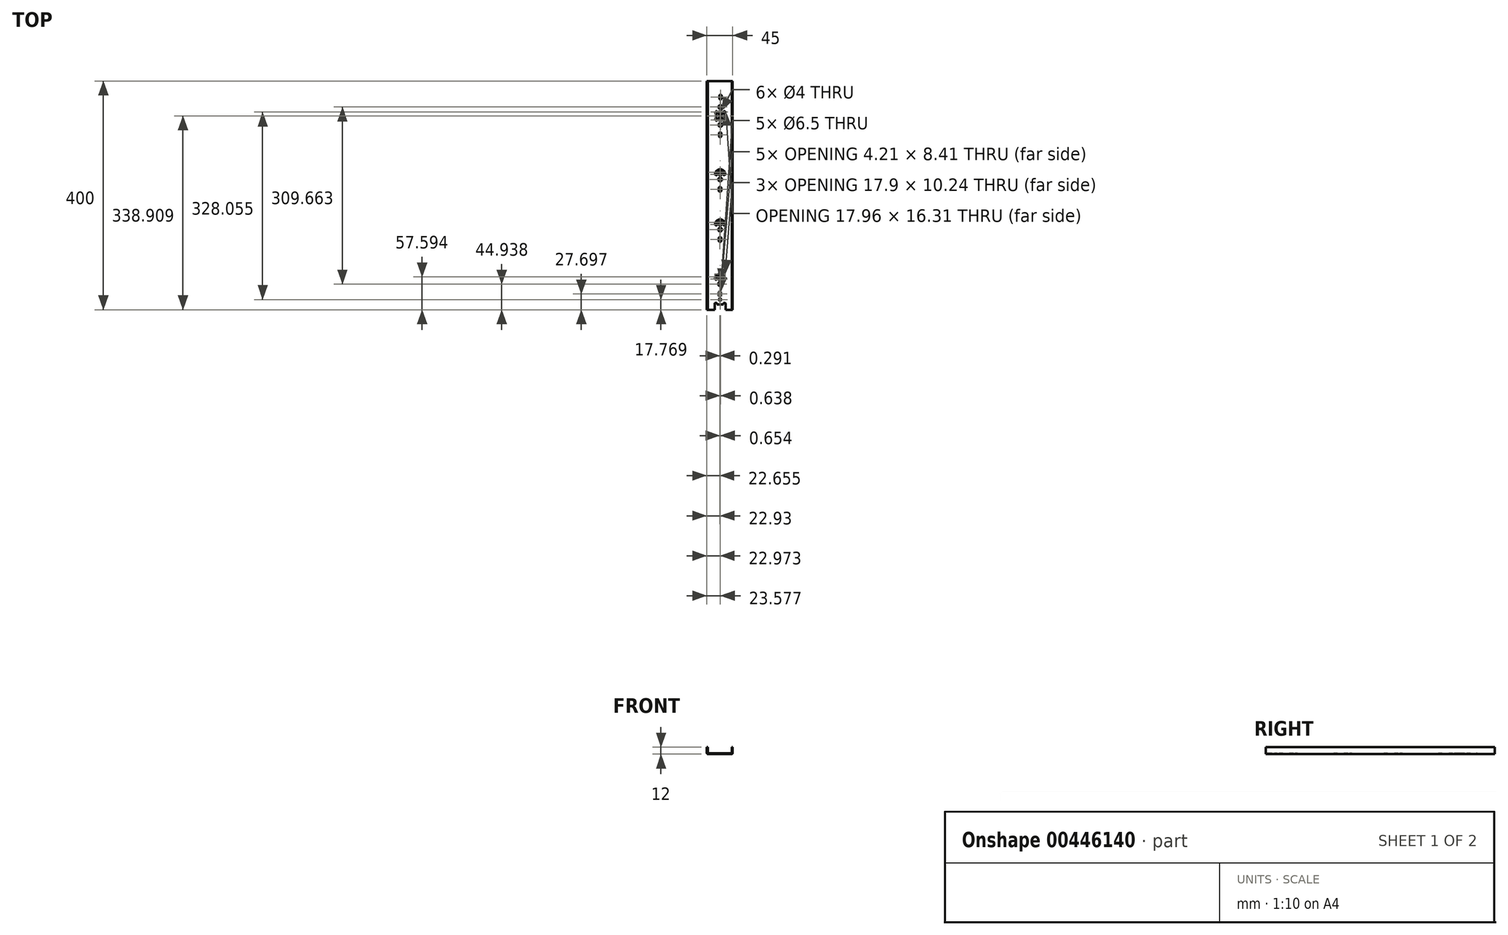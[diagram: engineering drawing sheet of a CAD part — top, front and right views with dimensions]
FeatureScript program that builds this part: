
annotation { "Feature Type Name" : "Feature", "Feature Type Description" : "" }
export const myFeature = defineFeature(function(context is Context, id is Id, definition is map)
    precondition{}
    {
        {
            var Q0;
            Q0=qCreatedBy(makeId("Front.planeOp"),FACE);
            var sketch = newSketch(context, id + "F0", { "sketchPlane" : qUnion([Q0])});
            skLineSegment(sketch, "E0", {"start": v(-48.01, 18) * mm, "end": v(-48.01, 8) * mm});
            skLineSegment(sketch, "E1", {"start": v(-5.01, 6) * mm, "end": v(-46.01, 6) * mm});
            skLineSegment(sketch, "E2", {"start": v(-3.01, 8) * mm, "end": v(-3.01, 18) * mm});
            skPoint(sketch, "E3.visualSharp", {"position": v(-48.01, 6) * mm});
            skArc(sketch, "E3.filletArc", {"start": v(-48.01, 8) * mm, "mid": v(-47.43, 6.59) * mm, "end": v(-46.01, 6) * mm});
            skPoint(sketch, "E4.visualSharp", {"position": v(-3.01, 6) * mm});
            skArc(sketch, "E4.filletArc", {"start": v(-5.01, 6) * mm, "mid": v(-3.6, 6.59) * mm, "end": v(-3.01, 8) * mm});
            skLineSegment(sketch, "E5.0", {"start": v(-46.52, 18) * mm, "end": v(-46.52, 8) * mm});
            skLineSegment(sketch, "E5.1", {"start": v(-4.5, 8) * mm, "end": v(-4.5, 18) * mm});
            skArc(sketch, "E5.2", {"start": v(-5.01, 7.5) * mm, "mid": v(-4.66, 7.64) * mm, "end": v(-4.5, 8) * mm});
            skLineSegment(sketch, "E5.3", {"start": v(-5.01, 7.5) * mm, "end": v(-46.01, 7.5) * mm});
            skArc(sketch, "E5.4", {"start": v(-46.52, 8) * mm, "mid": v(-46.37, 7.64) * mm, "end": v(-46.01, 7.5) * mm});
            skLineSegment(sketch, "E6", {"start": v(-48.01, 18) * mm, "end": v(-46.52, 18) * mm});
            skLineSegment(sketch, "E7", {"start": v(-4.5, 18) * mm, "end": v(-3.01, 18) * mm});
            skSolve(sketch);
        }
        {
            var Q0;
            Q0=makeQuery(id+"F0.imprint","IMPRINT",FACE,{"disambiguationData":[TD([[makeQuery(id+"F0.imprint","IMPRINT",EDGE,{"derivedFrom":sQuery(id+"F0.wireOp",EDGE,"E0")}),1.0]])]});
            extrude(context, id + "F1", {"entities" : qUnion([Q0]), "endBound" : BoundingType.SYMMETRIC, "depth" : 400 * mm});
        }
        {
            var Q0;
            Q0=qCreatedBy(makeId("Top.planeOp"),FACE);
            var sketch = newSketch(context, id + "F2", { "sketchPlane" : qUnion([Q0])});
            skLineSegment(sketch, "E8.top", {"start": v(-34.24, -200.48) * mm, "end": v(-15.31, -200.48) * mm});
            skLineSegment(sketch, "E8.left", {"start": v(-34.24, -189.04) * mm, "end": v(-34.24, -200.48) * mm});
            skLineSegment(sketch, "E8.right", {"start": v(-15.31, -189.04) * mm, "end": v(-15.31, -200.48) * mm});
            skPoint(sketch, "E8.middle", {"position": v(-24.78, -194.26) * mm});
            skLineSegment(sketch, "E9.top", {"start": v(-30.41, -190.8) * mm, "end": v(-18.97, -190.8) * mm});
            skLineSegment(sketch, "E9.left", {"start": v(-30.41, -189.04) * mm, "end": v(-30.41, -190.8) * mm});
            skLineSegment(sketch, "E9.right", {"start": v(-18.97, -189.04) * mm, "end": v(-18.97, -190.8) * mm});
            skLineSegment(sketch, "E10", {"start": v(-33.24, -188.04) * mm, "end": v(-31.41, -188.04) * mm});
            skLineSegment(sketch, "E11", {"start": v(-17.97, -188.04) * mm, "end": v(-16.31, -188.04) * mm});
            skPoint(sketch, "E12.visualSharp", {"position": v(-34.24, -188.04) * mm});
            skArc(sketch, "E12.filletArc", {"start": v(-33.24, -188.04) * mm, "mid": v(-33.95, -188.33) * mm, "end": v(-34.24, -189.04) * mm});
            skPoint(sketch, "E13.visualSharp", {"position": v(-30.41, -188.04) * mm});
            skArc(sketch, "E13.filletArc", {"start": v(-30.41, -189.04) * mm, "mid": v(-30.7, -188.33) * mm, "end": v(-31.41, -188.04) * mm});
            skPoint(sketch, "E14.visualSharp", {"position": v(-18.97, -188.04) * mm});
            skArc(sketch, "E14.filletArc", {"start": v(-17.97, -188.04) * mm, "mid": v(-18.68, -188.33) * mm, "end": v(-18.97, -189.04) * mm});
            skPoint(sketch, "E15.visualSharp", {"position": v(-15.31, -188.04) * mm});
            skArc(sketch, "E15.filletArc", {"start": v(-15.31, -189.04) * mm, "mid": v(-15.6, -188.33) * mm, "end": v(-16.31, -188.04) * mm});
            skCircle(sketch, "E16", {"center": v(-24.96, -182.23) * mm, "radius": 2 * mm});
            skPoint(sketch, "E17.startSnap0", {"position": v(-24.78, -200.48) * mm});
            skSolve(sketch);
        }
        {
            var Q0;
            Q0=makeQuery(id+"F2.imprint","IMPRINT",FACE,{"disambiguationData":[TD([[makeQuery(id+"F2.imprint","IMPRINT",EDGE,{"derivedFrom":sQuery(id+"F2.wireOp",EDGE,"E8.top")}),1.0]])]});
            var Q1;
            Q1=makeQuery(id+"F2.imprint","IMPRINT",FACE,{"disambiguationData":[TD([[makeQuery(id+"F2.imprint","IMPRINT",EDGE,{"derivedFrom":sQuery(id+"F2.wireOp",EDGE,"E16")}),1.0]])]});
            extrude(context, id + "F3", {"entities" : qUnion([Q0, Q1]), "operationType" : NewBodyOperationType.REMOVE, "endBound" : BoundingType.THROUGH_ALL, "depth" : 25 * mm});
        }
        {
            var Q0;
            Q0=qCreatedBy(makeId("Top.planeOp"),FACE);
            var sketch = newSketch(context, id + "F4", { "sketchPlane" : qUnion([Q0])});
            skLineSegment(sketch, "E18", {"start": v(-35.8, -180.96) * mm, "end": v(-32, -145.54) * mm});
            skLineSegment(sketch, "E19", {"start": v(-14.27, -180.96) * mm, "end": v(-18.08, -145.54) * mm});
            skArc(sketch, "E20", {"start": v(-18.08, -145.54) * mm, "mid": v(-25.04, -139.29) * mm, "end": v(-32, -145.54) * mm});
            skArc(sketch, "E21.0.startCap", {"start": v(-16.09, -145.32) * mm, "mid": v(-17.86, -147.53) * mm, "end": v(-20.07, -145.75) * mm});
            skArc(sketch, "E21.0.endCap", {"start": v(-30, -145.75) * mm, "mid": v(-32.21, -147.53) * mm, "end": v(-33.99, -145.32) * mm});
            skArc(sketch, "E21.0.left", {"start": v(-20.07, -145.75) * mm, "mid": v(-25.04, -141.29) * mm, "end": v(-30, -145.75) * mm});
            skArc(sketch, "E21.0.right", {"start": v(-16.09, -145.32) * mm, "mid": v(-25.04, -137.29) * mm, "end": v(-33.99, -145.32) * mm});
            skArc(sketch, "E21.1.startCap", {"start": v(-33.82, -181.17) * mm, "mid": v(-36.02, -182.95) * mm, "end": v(-37.8, -180.74) * mm});
            skArc(sketch, "E21.1.endCap", {"start": v(-33.99, -145.32) * mm, "mid": v(-31.78, -143.55) * mm, "end": v(-30, -145.75) * mm});
            skLineSegment(sketch, "E21.1.left", {"start": v(-37.8, -180.74) * mm, "end": v(-33.99, -145.32) * mm});
            skLineSegment(sketch, "E21.1.right", {"start": v(-33.82, -181.17) * mm, "end": v(-30, -145.75) * mm});
            skArc(sketch, "E21.2.startCap", {"start": v(-12.28, -180.74) * mm, "mid": v(-14.06, -182.95) * mm, "end": v(-16.26, -181.17) * mm});
            skArc(sketch, "E21.2.endCap", {"start": v(-20.07, -145.75) * mm, "mid": v(-18.3, -143.55) * mm, "end": v(-16.09, -145.32) * mm});
            skLineSegment(sketch, "E21.2.left", {"start": v(-16.26, -181.17) * mm, "end": v(-20.07, -145.75) * mm});
            skLineSegment(sketch, "E21.2.right", {"start": v(-12.28, -180.74) * mm, "end": v(-16.09, -145.32) * mm});
            skCircle(sketch, "E22", {"center": v(-25.04, -146.29) * mm, "radius": 2 * mm});
            skCircle(sketch, "E23", {"center": v(-25.08, -155.06) * mm, "radius": 3.25 * mm});
            skLineSegment(sketch, "E24.bottom", {"start": v(-25.25, -168.1) * mm, "end": v(-25.46, -168.1) * mm});
            skLineSegment(sketch, "E24.top", {"start": v(-25.25, -176.5) * mm, "end": v(-25.46, -176.5) * mm});
            skLineSegment(sketch, "E24.left", {"start": v(-23.25, -170.1) * mm, "end": v(-23.25, -174.5) * mm});
            skLineSegment(sketch, "E24.right", {"start": v(-27.46, -170.1) * mm, "end": v(-27.46, -174.5) * mm});
            skPoint(sketch, "E24.middle", {"position": v(-25.35, -172.3) * mm});
            skPoint(sketch, "E25.visualSharp", {"position": v(-27.46, -176.5) * mm});
            skArc(sketch, "E25.filletArc", {"start": v(-27.46, -174.5) * mm, "mid": v(-26.87, -175.92) * mm, "end": v(-25.46, -176.5) * mm});
            skPoint(sketch, "E26.visualSharp", {"position": v(-23.25, -176.5) * mm});
            skArc(sketch, "E26.filletArc", {"start": v(-25.25, -176.5) * mm, "mid": v(-23.84, -175.92) * mm, "end": v(-23.25, -174.5) * mm});
            skPoint(sketch, "E27.visualSharp", {"position": v(-23.25, -168.1) * mm});
            skArc(sketch, "E27.filletArc", {"start": v(-23.25, -170.1) * mm, "mid": v(-23.84, -168.68) * mm, "end": v(-25.25, -168.1) * mm});
            skPoint(sketch, "E28.visualSharp", {"position": v(-27.46, -168.1) * mm});
            skArc(sketch, "E28.filletArc", {"start": v(-25.46, -168.1) * mm, "mid": v(-26.87, -168.68) * mm, "end": v(-27.46, -170.1) * mm});
            skLineSegment(sketch, "E29", {"start": v(-35.51, -85.7) * mm, "end": v(-31.7, -50.29) * mm});
            skLineSegment(sketch, "E30", {"start": v(-13.98, -85.7) * mm, "end": v(-17.79, -50.29) * mm});
            skArc(sketch, "E31", {"start": v(-17.79, -50.29) * mm, "mid": v(-24.75, -44.03) * mm, "end": v(-31.7, -50.29) * mm});
            skArc(sketch, "E32.0.startCap", {"start": v(-15.8, -50.07) * mm, "mid": v(-17.57, -52.27) * mm, "end": v(-19.78, -50.5) * mm});
            skArc(sketch, "E32.0.endCap", {"start": v(-29.72, -50.5) * mm, "mid": v(-31.92, -52.27) * mm, "end": v(-33.7, -50.07) * mm});
            skArc(sketch, "E32.0.left", {"start": v(-19.78, -50.5) * mm, "mid": v(-24.75, -46.03) * mm, "end": v(-29.72, -50.5) * mm});
            skArc(sketch, "E32.0.right", {"start": v(-15.8, -50.07) * mm, "mid": v(-24.75, -42.03) * mm, "end": v(-33.7, -50.07) * mm});
            skArc(sketch, "E32.1.startCap", {"start": v(-33.53, -85.92) * mm, "mid": v(-35.73, -87.7) * mm, "end": v(-37.5, -85.5) * mm});
            skArc(sketch, "E32.1.endCap", {"start": v(-33.7, -50.07) * mm, "mid": v(-31.5, -48.3) * mm, "end": v(-29.72, -50.5) * mm});
            skLineSegment(sketch, "E32.1.left", {"start": v(-37.5, -85.5) * mm, "end": v(-33.7, -50.07) * mm});
            skLineSegment(sketch, "E32.1.right", {"start": v(-33.53, -85.92) * mm, "end": v(-29.72, -50.5) * mm});
            skArc(sketch, "E32.2.startCap", {"start": v(-12, -85.5) * mm, "mid": v(-13.77, -87.7) * mm, "end": v(-15.97, -85.92) * mm});
            skArc(sketch, "E32.2.endCap", {"start": v(-19.78, -50.5) * mm, "mid": v(-18, -48.3) * mm, "end": v(-15.8, -50.07) * mm});
            skLineSegment(sketch, "E32.2.left", {"start": v(-15.97, -85.92) * mm, "end": v(-19.78, -50.5) * mm});
            skLineSegment(sketch, "E32.2.right", {"start": v(-12, -85.5) * mm, "end": v(-15.8, -50.07) * mm});
            skCircle(sketch, "E33", {"center": v(-24.75, -51.03) * mm, "radius": 2 * mm});
            skCircle(sketch, "E34", {"center": v(-24.79, -59.81) * mm, "radius": 3.25 * mm});
            skLineSegment(sketch, "E35.bottom", {"start": v(-24.96, -72.84) * mm, "end": v(-25.17, -72.84) * mm});
            skLineSegment(sketch, "E35.top", {"start": v(-24.96, -81.26) * mm, "end": v(-25.17, -81.26) * mm});
            skLineSegment(sketch, "E35.left", {"start": v(-22.96, -74.84) * mm, "end": v(-22.96, -79.26) * mm});
            skLineSegment(sketch, "E35.right", {"start": v(-27.17, -74.84) * mm, "end": v(-27.17, -79.26) * mm});
            skPoint(sketch, "E35.middle", {"position": v(-25.06, -77.05) * mm});
            skPoint(sketch, "E36.visualSharp", {"position": v(-27.17, -81.26) * mm});
            skArc(sketch, "E36.filletArc", {"start": v(-27.17, -79.26) * mm, "mid": v(-26.58, -80.67) * mm, "end": v(-25.17, -81.26) * mm});
            skPoint(sketch, "E37.visualSharp", {"position": v(-22.96, -81.26) * mm});
            skArc(sketch, "E37.filletArc", {"start": v(-24.96, -81.26) * mm, "mid": v(-23.55, -80.67) * mm, "end": v(-22.96, -79.26) * mm});
            skPoint(sketch, "E38.visualSharp", {"position": v(-22.96, -72.84) * mm});
            skArc(sketch, "E38.filletArc", {"start": v(-22.96, -74.84) * mm, "mid": v(-23.55, -73.43) * mm, "end": v(-24.96, -72.84) * mm});
            skPoint(sketch, "E39.visualSharp", {"position": v(-27.17, -72.84) * mm});
            skArc(sketch, "E39.filletArc", {"start": v(-25.17, -72.84) * mm, "mid": v(-26.58, -73.43) * mm, "end": v(-27.17, -74.84) * mm});
            skLineSegment(sketch, "E40", {"start": v(-35.46, 2.07) * mm, "end": v(-31.65, 37.49) * mm});
            skLineSegment(sketch, "E41", {"start": v(-13.92, 2.07) * mm, "end": v(-17.73, 37.49) * mm});
            skArc(sketch, "E42", {"start": v(-17.73, 37.49) * mm, "mid": v(-24.7, 43.74) * mm, "end": v(-31.65, 37.49) * mm});
            skArc(sketch, "E43.0.startCap", {"start": v(-15.74, 37.7) * mm, "mid": v(-17.52, 35.5) * mm, "end": v(-19.72, 37.28) * mm});
            skArc(sketch, "E43.0.endCap", {"start": v(-29.66, 37.28) * mm, "mid": v(-31.86, 35.5) * mm, "end": v(-33.64, 37.7) * mm});
            skArc(sketch, "E43.0.left", {"start": v(-19.72, 37.28) * mm, "mid": v(-24.7, 41.74) * mm, "end": v(-29.66, 37.28) * mm});
            skArc(sketch, "E43.0.right", {"start": v(-15.74, 37.7) * mm, "mid": v(-24.7, 45.74) * mm, "end": v(-33.64, 37.7) * mm});
            skArc(sketch, "E43.1.startCap", {"start": v(-33.47, 1.86) * mm, "mid": v(-35.67, 0.08) * mm, "end": v(-37.45, 2.28) * mm});
            skArc(sketch, "E43.1.endCap", {"start": v(-33.64, 37.7) * mm, "mid": v(-31.44, 39.48) * mm, "end": v(-29.66, 37.28) * mm});
            skLineSegment(sketch, "E43.1.left", {"start": v(-37.45, 2.28) * mm, "end": v(-33.64, 37.7) * mm});
            skLineSegment(sketch, "E43.1.right", {"start": v(-33.47, 1.86) * mm, "end": v(-29.66, 37.28) * mm});
            skArc(sketch, "E43.2.startCap", {"start": v(-11.93, 2.28) * mm, "mid": v(-13.7, 0.08) * mm, "end": v(-15.91, 1.86) * mm});
            skArc(sketch, "E43.2.endCap", {"start": v(-19.72, 37.28) * mm, "mid": v(-17.94, 39.48) * mm, "end": v(-15.74, 37.7) * mm});
            skLineSegment(sketch, "E43.2.left", {"start": v(-15.91, 1.86) * mm, "end": v(-19.72, 37.28) * mm});
            skLineSegment(sketch, "E43.2.right", {"start": v(-11.93, 2.28) * mm, "end": v(-15.74, 37.7) * mm});
            skCircle(sketch, "E44", {"center": v(-24.7, 36.74) * mm, "radius": 2 * mm});
            skCircle(sketch, "E45", {"center": v(-24.73, 27.96) * mm, "radius": 3.25 * mm});
            skLineSegment(sketch, "E46.bottom", {"start": v(-24.9, 14.93) * mm, "end": v(-25.11, 14.93) * mm});
            skLineSegment(sketch, "E46.top", {"start": v(-24.9, 6.52) * mm, "end": v(-25.11, 6.52) * mm});
            skLineSegment(sketch, "E46.left", {"start": v(-22.9, 12.93) * mm, "end": v(-22.9, 8.52) * mm});
            skLineSegment(sketch, "E46.right", {"start": v(-27.11, 12.93) * mm, "end": v(-27.11, 8.52) * mm});
            skPoint(sketch, "E46.middle", {"position": v(-25, 10.72) * mm});
            skPoint(sketch, "E47.visualSharp", {"position": v(-27.11, 6.52) * mm});
            skArc(sketch, "E47.filletArc", {"start": v(-27.11, 8.52) * mm, "mid": v(-26.52, 7.1) * mm, "end": v(-25.11, 6.52) * mm});
            skPoint(sketch, "E48.visualSharp", {"position": v(-22.9, 6.52) * mm});
            skArc(sketch, "E48.filletArc", {"start": v(-24.9, 6.52) * mm, "mid": v(-23.49, 7.1) * mm, "end": v(-22.9, 8.52) * mm});
            skPoint(sketch, "E49.visualSharp", {"position": v(-22.9, 14.93) * mm});
            skArc(sketch, "E49.filletArc", {"start": v(-22.9, 12.93) * mm, "mid": v(-23.49, 14.35) * mm, "end": v(-24.9, 14.93) * mm});
            skPoint(sketch, "E50.visualSharp", {"position": v(-27.11, 14.93) * mm});
            skArc(sketch, "E50.filletArc", {"start": v(-25.11, 14.93) * mm, "mid": v(-26.52, 14.35) * mm, "end": v(-27.11, 12.93) * mm});
            skLineSegment(sketch, "E51", {"start": v(-35.17, 97.32) * mm, "end": v(-31.36, 132.74) * mm});
            skLineSegment(sketch, "E52", {"start": v(-13.63, 97.32) * mm, "end": v(-17.44, 132.74) * mm});
            skArc(sketch, "E53", {"start": v(-17.44, 132.74) * mm, "mid": v(-24.4, 139) * mm, "end": v(-31.36, 132.74) * mm});
            skArc(sketch, "E54.0.startCap", {"start": v(-15.45, 132.96) * mm, "mid": v(-17.23, 130.75) * mm, "end": v(-19.43, 132.53) * mm});
            skArc(sketch, "E54.0.endCap", {"start": v(-29.37, 132.53) * mm, "mid": v(-31.57, 130.75) * mm, "end": v(-33.35, 132.96) * mm});
            skArc(sketch, "E54.0.left", {"start": v(-19.43, 132.53) * mm, "mid": v(-24.4, 137) * mm, "end": v(-29.37, 132.53) * mm});
            skArc(sketch, "E54.0.right", {"start": v(-15.45, 132.96) * mm, "mid": v(-24.4, 141) * mm, "end": v(-33.35, 132.96) * mm});
            skArc(sketch, "E54.1.startCap", {"start": v(-33.18, 97.1) * mm, "mid": v(-35.38, 95.33) * mm, "end": v(-37.16, 97.54) * mm});
            skArc(sketch, "E54.1.endCap", {"start": v(-33.35, 132.96) * mm, "mid": v(-31.15, 134.73) * mm, "end": v(-29.37, 132.53) * mm});
            skLineSegment(sketch, "E54.1.left", {"start": v(-37.16, 97.54) * mm, "end": v(-33.35, 132.96) * mm});
            skLineSegment(sketch, "E54.1.right", {"start": v(-33.18, 97.1) * mm, "end": v(-29.37, 132.53) * mm});
            skArc(sketch, "E54.2.startCap", {"start": v(-11.64, 97.54) * mm, "mid": v(-13.42, 95.33) * mm, "end": v(-15.62, 97.1) * mm});
            skArc(sketch, "E54.2.endCap", {"start": v(-19.43, 132.53) * mm, "mid": v(-17.65, 134.73) * mm, "end": v(-15.45, 132.96) * mm});
            skLineSegment(sketch, "E54.2.left", {"start": v(-15.62, 97.1) * mm, "end": v(-19.43, 132.53) * mm});
            skLineSegment(sketch, "E54.2.right", {"start": v(-11.64, 97.54) * mm, "end": v(-15.45, 132.96) * mm});
            skCircle(sketch, "E55", {"center": v(-24.4, 132) * mm, "radius": 2 * mm});
            skCircle(sketch, "E56", {"center": v(-24.44, 123.22) * mm, "radius": 3.25 * mm});
            skLineSegment(sketch, "E57.bottom", {"start": v(-24.61, 110.18) * mm, "end": v(-24.82, 110.18) * mm});
            skLineSegment(sketch, "E57.top", {"start": v(-24.61, 101.77) * mm, "end": v(-24.82, 101.77) * mm});
            skLineSegment(sketch, "E57.left", {"start": v(-22.61, 108.18) * mm, "end": v(-22.61, 103.77) * mm});
            skLineSegment(sketch, "E57.right", {"start": v(-26.82, 108.18) * mm, "end": v(-26.82, 103.77) * mm});
            skPoint(sketch, "E57.middle", {"position": v(-24.72, 105.98) * mm});
            skPoint(sketch, "E58.visualSharp", {"position": v(-26.82, 101.77) * mm});
            skArc(sketch, "E58.filletArc", {"start": v(-26.82, 103.77) * mm, "mid": v(-26.23, 102.36) * mm, "end": v(-24.82, 101.77) * mm});
            skPoint(sketch, "E59.visualSharp", {"position": v(-22.61, 101.77) * mm});
            skArc(sketch, "E59.filletArc", {"start": v(-24.61, 101.77) * mm, "mid": v(-23.2, 102.36) * mm, "end": v(-22.61, 103.77) * mm});
            skPoint(sketch, "E60.visualSharp", {"position": v(-22.61, 110.18) * mm});
            skArc(sketch, "E60.filletArc", {"start": v(-22.61, 108.18) * mm, "mid": v(-23.2, 109.6) * mm, "end": v(-24.61, 110.18) * mm});
            skPoint(sketch, "E61.visualSharp", {"position": v(-26.82, 110.18) * mm});
            skArc(sketch, "E61.filletArc", {"start": v(-24.82, 110.18) * mm, "mid": v(-26.23, 109.6) * mm, "end": v(-26.82, 108.18) * mm});
            skLineSegment(sketch, "E62", {"start": v(-13.7, 180.5) * mm, "end": v(-17.5, 145.08) * mm});
            skLineSegment(sketch, "E63", {"start": v(-35.23, 180.5) * mm, "end": v(-31.43, 145.08) * mm});
            skArc(sketch, "E64", {"start": v(-31.43, 145.08) * mm, "mid": v(-24.47, 138.82) * mm, "end": v(-17.5, 145.08) * mm});
            skArc(sketch, "E65.0.startCap", {"start": v(-33.42, 144.86) * mm, "mid": v(-31.64, 147.06) * mm, "end": v(-29.44, 145.29) * mm});
            skArc(sketch, "E65.0.endCap", {"start": v(-19.5, 145.29) * mm, "mid": v(-17.3, 147.06) * mm, "end": v(-15.52, 144.86) * mm});
            skArc(sketch, "E65.0.left", {"start": v(-29.44, 145.29) * mm, "mid": v(-24.47, 140.82) * mm, "end": v(-19.5, 145.29) * mm});
            skArc(sketch, "E65.0.right", {"start": v(-33.42, 144.86) * mm, "mid": v(-24.47, 136.82) * mm, "end": v(-15.52, 144.86) * mm});
            skArc(sketch, "E65.1.startCap", {"start": v(-15.69, 180.7) * mm, "mid": v(-13.49, 182.48) * mm, "end": v(-11.71, 180.28) * mm});
            skArc(sketch, "E65.1.endCap", {"start": v(-15.52, 144.86) * mm, "mid": v(-17.72, 143.09) * mm, "end": v(-19.5, 145.29) * mm});
            skLineSegment(sketch, "E65.1.left", {"start": v(-11.71, 180.28) * mm, "end": v(-15.52, 144.86) * mm});
            skLineSegment(sketch, "E65.1.right", {"start": v(-15.69, 180.7) * mm, "end": v(-19.5, 145.29) * mm});
            skArc(sketch, "E65.2.startCap", {"start": v(-37.22, 180.28) * mm, "mid": v(-35.45, 182.48) * mm, "end": v(-33.25, 180.7) * mm});
            skArc(sketch, "E65.2.endCap", {"start": v(-29.44, 145.29) * mm, "mid": v(-31.21, 143.09) * mm, "end": v(-33.42, 144.86) * mm});
            skLineSegment(sketch, "E65.2.left", {"start": v(-33.25, 180.7) * mm, "end": v(-29.44, 145.29) * mm});
            skLineSegment(sketch, "E65.2.right", {"start": v(-37.22, 180.28) * mm, "end": v(-33.42, 144.86) * mm});
            skCircle(sketch, "E66", {"center": v(-24.47, 145.82) * mm, "radius": 2 * mm});
            skCircle(sketch, "E67", {"center": v(-24.43, 154.6) * mm, "radius": 3.25 * mm});
            skLineSegment(sketch, "E68.bottom", {"start": v(-24.25, 167.63) * mm, "end": v(-24.05, 167.63) * mm});
            skLineSegment(sketch, "E68.top", {"start": v(-24.25, 176.05) * mm, "end": v(-24.05, 176.05) * mm});
            skLineSegment(sketch, "E68.left", {"start": v(-26.25, 169.63) * mm, "end": v(-26.25, 174.05) * mm});
            skLineSegment(sketch, "E68.right", {"start": v(-22.05, 169.63) * mm, "end": v(-22.05, 174.05) * mm});
            skPoint(sketch, "E68.middle", {"position": v(-24.15, 171.84) * mm});
            skPoint(sketch, "E69.visualSharp", {"position": v(-22.05, 176.05) * mm});
            skArc(sketch, "E69.filletArc", {"start": v(-22.05, 174.05) * mm, "mid": v(-22.63, 175.46) * mm, "end": v(-24.05, 176.05) * mm});
            skPoint(sketch, "E70.visualSharp", {"position": v(-26.25, 176.05) * mm});
            skArc(sketch, "E70.filletArc", {"start": v(-24.25, 176.05) * mm, "mid": v(-25.67, 175.46) * mm, "end": v(-26.25, 174.05) * mm});
            skPoint(sketch, "E71.visualSharp", {"position": v(-26.25, 167.63) * mm});
            skArc(sketch, "E71.filletArc", {"start": v(-26.25, 169.63) * mm, "mid": v(-25.67, 168.22) * mm, "end": v(-24.25, 167.63) * mm});
            skPoint(sketch, "E72.visualSharp", {"position": v(-22.05, 167.63) * mm});
            skArc(sketch, "E72.filletArc", {"start": v(-24.05, 167.63) * mm, "mid": v(-22.63, 168.22) * mm, "end": v(-22.05, 169.63) * mm});
            skSolve(sketch);
        }
        {
            var Q0;
            Q0=makeQuery(id+"F4.imprint","IMPRINT",FACE,{"disambiguationData":[TD([[makeQuery(id+"F4.imprint","IMPRINT",EDGE,{"derivedFrom":sQuery(id+"F4.wireOp",EDGE,"E68.bottom")}),1.0]])]});
            var Q1;
            Q1=makeQuery(id+"F4.imprint","IMPRINT",FACE,{"disambiguationData":[TD([[makeQuery(id+"F4.imprint","IMPRINT",EDGE,{"derivedFrom":sQuery(id+"F4.wireOp",EDGE,"E65.2.startCap")}),-1.0]])]});
            var Q2;
            {var subQ0=sQuery(id+"F4.wireOp",EDGE,"E65.0.right");var subQ1=sQuery(id+"F4.wireOp",EDGE,"E54.0.right");var subQ2=makeQuery(id+"F4.imprint","INTERSECT",VERTEX,{"disambiguationData":[OD(1.0)],"derivedFrom":[subQ1,subQ0]});Q2=makeQuery(id+"F4.imprint","IMPRINT",FACE,{"disambiguationData":[TD([[makeQuery(id+"F4.imprint","IMPRINT",EDGE,{"disambiguationData":[TD([[subQ2,1.0]])],"derivedFrom":subQ1}),-1.0]])]});}
            var Q3;
            {var subQ0=sQuery(id+"F4.wireOp",EDGE,"E65.0.left");var subQ1=sQuery(id+"F4.wireOp",EDGE,"E54.0.right");var subQ2=makeQuery(id+"F4.imprint","INTERSECT",VERTEX,{"disambiguationData":[OD(1.0)],"derivedFrom":[subQ1,subQ0]});Q3=makeQuery(id+"F4.imprint","IMPRINT",FACE,{"disambiguationData":[TD([[makeQuery(id+"F4.imprint","IMPRINT",EDGE,{"disambiguationData":[TD([[subQ2,-1.0]])],"derivedFrom":subQ1}),-1.0]])]});}
            var Q4;
            {var subQ0=sQuery(id+"F4.wireOp",EDGE,"E64");var subQ1=sQuery(id+"F4.wireOp",EDGE,"E63");var subQ2=makeQuery(id+"F4.imprint","INTERSECT",VERTEX,{"derivedFrom":[subQ1,subQ0]});Q4=makeQuery(id+"F4.imprint","IMPRINT",FACE,{"disambiguationData":[TD([[makeQuery(id+"F4.imprint","IMPRINT",EDGE,{"disambiguationData":[TD([[subQ2,1.0]])],"derivedFrom":subQ1}),1.0]])]});}
            var Q5;
            {var subQ0=sQuery(id+"F4.wireOp",EDGE,"E64");var subQ1=sQuery(id+"F4.wireOp",EDGE,"E63");var subQ2=makeQuery(id+"F4.imprint","INTERSECT",VERTEX,{"derivedFrom":[subQ1,subQ0]});Q5=makeQuery(id+"F4.imprint","IMPRINT",FACE,{"disambiguationData":[TD([[makeQuery(id+"F4.imprint","IMPRINT",EDGE,{"disambiguationData":[TD([[subQ2,1.0]])],"derivedFrom":subQ1}),-1.0]])]});}
            var Q6;
            Q6=makeQuery(id+"F4.imprint","IMPRINT",FACE,{"disambiguationData":[TD([[makeQuery(id+"F4.imprint","IMPRINT",EDGE,{"derivedFrom":sQuery(id+"F4.wireOp",EDGE,"E66")}),1.0]])]});
            var Q7;
            {var subQ0=sQuery(id+"F4.wireOp",EDGE,"E64");var subQ1=sQuery(id+"F4.wireOp",EDGE,"E62");var subQ2=makeQuery(id+"F4.imprint","INTERSECT",VERTEX,{"derivedFrom":[subQ1,subQ0]});Q7=makeQuery(id+"F4.imprint","IMPRINT",FACE,{"disambiguationData":[TD([[makeQuery(id+"F4.imprint","IMPRINT",EDGE,{"disambiguationData":[TD([[subQ2,1.0]])],"derivedFrom":subQ1}),-1.0]])]});}
            var Q8;
            {var subQ0=sQuery(id+"F4.wireOp",EDGE,"E64");var subQ1=sQuery(id+"F4.wireOp",EDGE,"E62");var subQ2=makeQuery(id+"F4.imprint","INTERSECT",VERTEX,{"derivedFrom":[subQ1,subQ0]});Q8=makeQuery(id+"F4.imprint","IMPRINT",FACE,{"disambiguationData":[TD([[makeQuery(id+"F4.imprint","IMPRINT",EDGE,{"disambiguationData":[TD([[subQ2,1.0]])],"derivedFrom":subQ1}),1.0]])]});}
            var Q9;
            Q9=makeQuery(id+"F4.imprint","IMPRINT",FACE,{"disambiguationData":[TD([[makeQuery(id+"F4.imprint","IMPRINT",EDGE,{"derivedFrom":sQuery(id+"F4.wireOp",EDGE,"E65.1.startCap")}),-1.0]])]});
            var Q10;
            Q10=makeQuery(id+"F4.imprint","IMPRINT",FACE,{"disambiguationData":[TD([[makeQuery(id+"F4.imprint","IMPRINT",EDGE,{"derivedFrom":sQuery(id+"F4.wireOp",EDGE,"E67")}),1.0]])]});
            var Q11;
            {var subQ0=sQuery(id+"F4.wireOp",EDGE,"E65.0.left");var subQ1=sQuery(id+"F4.wireOp",EDGE,"E54.0.right");var subQ2=makeQuery(id+"F4.imprint","INTERSECT",VERTEX,{"disambiguationData":[OD(0.0)],"derivedFrom":[subQ1,subQ0]});Q11=makeQuery(id+"F4.imprint","IMPRINT",FACE,{"disambiguationData":[TD([[makeQuery(id+"F4.imprint","IMPRINT",EDGE,{"disambiguationData":[TD([[subQ2,1.0]])],"derivedFrom":subQ1}),-1.0]])]});}
            var Q12;
            {var subQ0=sQuery(id+"F4.wireOp",EDGE,"E65.0.right");var subQ1=sQuery(id+"F4.wireOp",EDGE,"E54.0.right");var subQ2=makeQuery(id+"F4.imprint","INTERSECT",VERTEX,{"disambiguationData":[OD(0.0)],"derivedFrom":[subQ1,subQ0]});Q12=makeQuery(id+"F4.imprint","IMPRINT",FACE,{"disambiguationData":[TD([[makeQuery(id+"F4.imprint","IMPRINT",EDGE,{"disambiguationData":[TD([[subQ2,-1.0]])],"derivedFrom":subQ1}),-1.0]])]});}
            var Q13;
            {var subQ0=sQuery(id+"F4.wireOp",EDGE,"E64");var subQ1=sQuery(id+"F4.wireOp",EDGE,"E53");var subQ9=makeQuery(id+"F4.imprint","INTERSECT",VERTEX,{"disambiguationData":[OD(0.0)],"derivedFrom":[subQ1,subQ0]});Q13=makeQuery(id+"F4.imprint","IMPRINT",FACE,{"disambiguationData":[TD([[makeQuery(id+"F4.imprint","IMPRINT",EDGE,{"disambiguationData":[TD([[subQ9,-1.0]])],"derivedFrom":subQ1}),-1.0]])]});}
            var Q14;
            {var subQ0=sQuery(id+"F4.wireOp",EDGE,"E64");var subQ1=sQuery(id+"F4.wireOp",EDGE,"E53");var subQ2=makeQuery(id+"F4.imprint","INTERSECT",VERTEX,{"disambiguationData":[OD(1.0)],"derivedFrom":[subQ1,subQ0]});Q14=makeQuery(id+"F4.imprint","IMPRINT",FACE,{"disambiguationData":[TD([[makeQuery(id+"F4.imprint","IMPRINT",EDGE,{"disambiguationData":[TD([[subQ2,-1.0]])],"derivedFrom":subQ1}),-1.0]])]});}
            var Q15;
            {var subQ1=sQuery(id+"F4.wireOp",EDGE,"E53");var subQ4=sQuery(id+"F4.wireOp",EDGE,"E65.0.right");var subQ9=makeQuery(id+"F4.imprint","INTERSECT",VERTEX,{"disambiguationData":[OD(0.0)],"derivedFrom":[subQ1,subQ4]});Q15=makeQuery(id+"F4.imprint","IMPRINT",FACE,{"disambiguationData":[TD([[makeQuery(id+"F4.imprint","IMPRINT",EDGE,{"disambiguationData":[TD([[subQ9,-1.0]])],"derivedFrom":subQ1}),1.0]])]});}
            var Q16;
            {var subQ0=sQuery(id+"F4.wireOp",EDGE,"E65.0.right");var subQ1=sQuery(id+"F4.wireOp",EDGE,"E53");var subQ2=makeQuery(id+"F4.imprint","INTERSECT",VERTEX,{"disambiguationData":[OD(0.0)],"derivedFrom":[subQ1,subQ0]});Q16=makeQuery(id+"F4.imprint","IMPRINT",FACE,{"disambiguationData":[TD([[makeQuery(id+"F4.imprint","IMPRINT",EDGE,{"disambiguationData":[TD([[subQ2,-1.0]])],"derivedFrom":subQ1}),-1.0]])]});}
            var Q17;
            {var subQ0=sQuery(id+"F4.wireOp",EDGE,"E65.0.right");var subQ1=sQuery(id+"F4.wireOp",EDGE,"E53");var subQ2=makeQuery(id+"F4.imprint","INTERSECT",VERTEX,{"disambiguationData":[OD(1.0)],"derivedFrom":[subQ1,subQ0]});Q17=makeQuery(id+"F4.imprint","IMPRINT",FACE,{"disambiguationData":[TD([[makeQuery(id+"F4.imprint","IMPRINT",EDGE,{"disambiguationData":[TD([[subQ2,-1.0]])],"derivedFrom":subQ1}),1.0]])]});}
            var Q18;
            {var subQ0=sQuery(id+"F4.wireOp",EDGE,"E65.0.right");var subQ1=sQuery(id+"F4.wireOp",EDGE,"E53");var subQ2=makeQuery(id+"F4.imprint","INTERSECT",VERTEX,{"disambiguationData":[OD(1.0)],"derivedFrom":[subQ1,subQ0]});Q18=makeQuery(id+"F4.imprint","IMPRINT",FACE,{"disambiguationData":[TD([[makeQuery(id+"F4.imprint","IMPRINT",EDGE,{"disambiguationData":[TD([[subQ2,-1.0]])],"derivedFrom":subQ1}),-1.0]])]});}
            var Q19;
            {var subQ0=sQuery(id+"F4.wireOp",EDGE,"E54.2.endCap");var subQ1=sQuery(id+"F4.wireOp",EDGE,"E53");var subQ2=makeQuery(id+"F4.imprint","INTERSECT",VERTEX,{"derivedFrom":[subQ1,subQ0]});Q19=makeQuery(id+"F4.imprint","IMPRINT",FACE,{"disambiguationData":[TD([[makeQuery(id+"F4.imprint","IMPRINT",EDGE,{"disambiguationData":[TD([[subQ2,-1.0]])],"derivedFrom":subQ1}),1.0]])]});}
            var Q20;
            {var subQ0=sQuery(id+"F4.wireOp",EDGE,"E54.2.endCap");var subQ1=sQuery(id+"F4.wireOp",EDGE,"E53");var subQ2=makeQuery(id+"F4.imprint","INTERSECT",VERTEX,{"derivedFrom":[subQ1,subQ0]});Q20=makeQuery(id+"F4.imprint","IMPRINT",FACE,{"disambiguationData":[TD([[makeQuery(id+"F4.imprint","IMPRINT",EDGE,{"disambiguationData":[TD([[subQ2,-1.0]])],"derivedFrom":subQ1}),-1.0]])]});}
            var Q21;
            {var subQ0=sQuery(id+"F4.wireOp",EDGE,"E64");var subQ1=sQuery(id+"F4.wireOp",EDGE,"E53");var subQ2=makeQuery(id+"F4.imprint","INTERSECT",VERTEX,{"disambiguationData":[OD(0.0)],"derivedFrom":[subQ1,subQ0]});Q21=makeQuery(id+"F4.imprint","IMPRINT",FACE,{"disambiguationData":[TD([[makeQuery(id+"F4.imprint","IMPRINT",EDGE,{"disambiguationData":[TD([[subQ2,-1.0]])],"derivedFrom":subQ1}),1.0]])]});}
            var Q22;
            {var subQ0=sQuery(id+"F4.wireOp",EDGE,"E53");var subQ1=sQuery(id+"F4.wireOp",EDGE,"E52");var subQ2=makeQuery(id+"F4.imprint","INTERSECT",VERTEX,{"derivedFrom":[subQ1,subQ0]});Q22=makeQuery(id+"F4.imprint","IMPRINT",FACE,{"disambiguationData":[TD([[makeQuery(id+"F4.imprint","IMPRINT",EDGE,{"disambiguationData":[TD([[subQ2,1.0]])],"derivedFrom":subQ1}),1.0]])]});}
            var Q23;
            {var subQ0=sQuery(id+"F4.wireOp",EDGE,"E53");var subQ1=sQuery(id+"F4.wireOp",EDGE,"E52");var subQ2=makeQuery(id+"F4.imprint","INTERSECT",VERTEX,{"derivedFrom":[subQ1,subQ0]});Q23=makeQuery(id+"F4.imprint","IMPRINT",FACE,{"disambiguationData":[TD([[makeQuery(id+"F4.imprint","IMPRINT",EDGE,{"disambiguationData":[TD([[subQ2,1.0]])],"derivedFrom":subQ1}),-1.0]])]});}
            var Q24;
            Q24=makeQuery(id+"F4.imprint","IMPRINT",FACE,{"disambiguationData":[TD([[makeQuery(id+"F4.imprint","IMPRINT",EDGE,{"derivedFrom":sQuery(id+"F4.wireOp",EDGE,"E54.2.startCap")}),-1.0]])]});
            var Q25;
            Q25=makeQuery(id+"F4.imprint","IMPRINT",FACE,{"disambiguationData":[TD([[makeQuery(id+"F4.imprint","IMPRINT",EDGE,{"derivedFrom":sQuery(id+"F4.wireOp",EDGE,"E56")}),1.0]])]});
            var Q26;
            Q26=makeQuery(id+"F4.imprint","IMPRINT",FACE,{"disambiguationData":[TD([[makeQuery(id+"F4.imprint","IMPRINT",EDGE,{"derivedFrom":sQuery(id+"F4.wireOp",EDGE,"E55")}),1.0]])]});
            var Q27;
            {var subQ0=sQuery(id+"F4.wireOp",EDGE,"E53");var subQ1=sQuery(id+"F4.wireOp",EDGE,"E51");var subQ2=makeQuery(id+"F4.imprint","INTERSECT",VERTEX,{"derivedFrom":[subQ1,subQ0]});Q27=makeQuery(id+"F4.imprint","IMPRINT",FACE,{"disambiguationData":[TD([[makeQuery(id+"F4.imprint","IMPRINT",EDGE,{"disambiguationData":[TD([[subQ2,1.0]])],"derivedFrom":subQ1}),1.0]])]});}
            var Q28;
            {var subQ0=sQuery(id+"F4.wireOp",EDGE,"E53");var subQ1=sQuery(id+"F4.wireOp",EDGE,"E51");var subQ2=makeQuery(id+"F4.imprint","INTERSECT",VERTEX,{"derivedFrom":[subQ1,subQ0]});Q28=makeQuery(id+"F4.imprint","IMPRINT",FACE,{"disambiguationData":[TD([[makeQuery(id+"F4.imprint","IMPRINT",EDGE,{"disambiguationData":[TD([[subQ2,1.0]])],"derivedFrom":subQ1}),-1.0]])]});}
            var Q29;
            Q29=makeQuery(id+"F4.imprint","IMPRINT",FACE,{"disambiguationData":[TD([[makeQuery(id+"F4.imprint","IMPRINT",EDGE,{"derivedFrom":sQuery(id+"F4.wireOp",EDGE,"E54.1.startCap")}),-1.0]])]});
            var Q30;
            Q30=makeQuery(id+"F4.imprint","IMPRINT",FACE,{"disambiguationData":[TD([[makeQuery(id+"F4.imprint","IMPRINT",EDGE,{"derivedFrom":sQuery(id+"F4.wireOp",EDGE,"E57.bottom")}),1.0]])]});
            var Q31;
            Q31=makeQuery(id+"F4.imprint","IMPRINT",FACE,{"disambiguationData":[TD([[makeQuery(id+"F4.imprint","IMPRINT",EDGE,{"derivedFrom":sQuery(id+"F4.wireOp",EDGE,"E43.1.startCap")}),-1.0]])]});
            var Q32;
            Q32=makeQuery(id+"F4.imprint","IMPRINT",FACE,{"disambiguationData":[TD([[makeQuery(id+"F4.imprint","IMPRINT",EDGE,{"derivedFrom":sQuery(id+"F4.wireOp",EDGE,"E46.bottom")}),1.0]])]});
            var Q33;
            Q33=makeQuery(id+"F4.imprint","IMPRINT",FACE,{"disambiguationData":[TD([[makeQuery(id+"F4.imprint","IMPRINT",EDGE,{"derivedFrom":sQuery(id+"F4.wireOp",EDGE,"E43.2.startCap")}),-1.0]])]});
            var Q34;
            Q34=makeQuery(id+"F4.imprint","IMPRINT",FACE,{"disambiguationData":[TD([[makeQuery(id+"F4.imprint","IMPRINT",EDGE,{"derivedFrom":sQuery(id+"F4.wireOp",EDGE,"E45")}),1.0]])]});
            var Q35;
            Q35=makeQuery(id+"F4.imprint","IMPRINT",FACE,{"disambiguationData":[TD([[makeQuery(id+"F4.imprint","IMPRINT",EDGE,{"derivedFrom":sQuery(id+"F4.wireOp",EDGE,"E44")}),1.0]])]});
            var Q36;
            {var subQ5=sQuery(id+"F4.wireOp",EDGE,"E43.0.left");Q36=makeQuery(id+"F4.imprint","IMPRINT",FACE,{"disambiguationData":[TD([[makeQuery(id+"F4.imprint","IMPRINT",EDGE,{"derivedFrom":subQ5}),-1.0]])]});}
            var Q37;
            {var subQ5=sQuery(id+"F4.wireOp",EDGE,"E43.0.right");Q37=makeQuery(id+"F4.imprint","IMPRINT",FACE,{"disambiguationData":[TD([[makeQuery(id+"F4.imprint","IMPRINT",EDGE,{"derivedFrom":subQ5}),1.0]])]});}
            var Q38;
            {var subQ0=sQuery(id+"F4.wireOp",EDGE,"E42");var subQ1=sQuery(id+"F4.wireOp",EDGE,"E41");var subQ2=makeQuery(id+"F4.imprint","INTERSECT",VERTEX,{"derivedFrom":[subQ1,subQ0]});Q38=makeQuery(id+"F4.imprint","IMPRINT",FACE,{"disambiguationData":[TD([[makeQuery(id+"F4.imprint","IMPRINT",EDGE,{"disambiguationData":[TD([[subQ2,1.0]])],"derivedFrom":subQ1}),1.0]])]});}
            var Q39;
            {var subQ0=sQuery(id+"F4.wireOp",EDGE,"E42");var subQ1=sQuery(id+"F4.wireOp",EDGE,"E41");var subQ2=makeQuery(id+"F4.imprint","INTERSECT",VERTEX,{"derivedFrom":[subQ1,subQ0]});Q39=makeQuery(id+"F4.imprint","IMPRINT",FACE,{"disambiguationData":[TD([[makeQuery(id+"F4.imprint","IMPRINT",EDGE,{"disambiguationData":[TD([[subQ2,1.0]])],"derivedFrom":subQ1}),-1.0]])]});}
            var Q40;
            {var subQ0=sQuery(id+"F4.wireOp",EDGE,"E42");var subQ1=sQuery(id+"F4.wireOp",EDGE,"E40");var subQ2=makeQuery(id+"F4.imprint","INTERSECT",VERTEX,{"derivedFrom":[subQ1,subQ0]});Q40=makeQuery(id+"F4.imprint","IMPRINT",FACE,{"disambiguationData":[TD([[makeQuery(id+"F4.imprint","IMPRINT",EDGE,{"disambiguationData":[TD([[subQ2,1.0]])],"derivedFrom":subQ1}),1.0]])]});}
            var Q41;
            {var subQ0=sQuery(id+"F4.wireOp",EDGE,"E42");var subQ1=sQuery(id+"F4.wireOp",EDGE,"E40");var subQ2=makeQuery(id+"F4.imprint","INTERSECT",VERTEX,{"derivedFrom":[subQ1,subQ0]});Q41=makeQuery(id+"F4.imprint","IMPRINT",FACE,{"disambiguationData":[TD([[makeQuery(id+"F4.imprint","IMPRINT",EDGE,{"disambiguationData":[TD([[subQ2,1.0]])],"derivedFrom":subQ1}),-1.0]])]});}
            var Q42;
            Q42=makeQuery(id+"F4.imprint","IMPRINT",FACE,{"disambiguationData":[TD([[makeQuery(id+"F4.imprint","IMPRINT",EDGE,{"derivedFrom":sQuery(id+"F4.wireOp",EDGE,"E32.1.startCap")}),-1.0]])]});
            var Q43;
            Q43=makeQuery(id+"F4.imprint","IMPRINT",FACE,{"disambiguationData":[TD([[makeQuery(id+"F4.imprint","IMPRINT",EDGE,{"derivedFrom":sQuery(id+"F4.wireOp",EDGE,"E32.2.startCap")}),-1.0]])]});
            var Q44;
            Q44=makeQuery(id+"F4.imprint","IMPRINT",FACE,{"disambiguationData":[TD([[makeQuery(id+"F4.imprint","IMPRINT",EDGE,{"derivedFrom":sQuery(id+"F4.wireOp",EDGE,"E35.bottom")}),1.0]])]});
            var Q45;
            Q45=makeQuery(id+"F4.imprint","IMPRINT",FACE,{"disambiguationData":[TD([[makeQuery(id+"F4.imprint","IMPRINT",EDGE,{"derivedFrom":sQuery(id+"F4.wireOp",EDGE,"E34")}),1.0]])]});
            var Q46;
            Q46=makeQuery(id+"F4.imprint","IMPRINT",FACE,{"disambiguationData":[TD([[makeQuery(id+"F4.imprint","IMPRINT",EDGE,{"derivedFrom":sQuery(id+"F4.wireOp",EDGE,"E33")}),1.0]])]});
            var Q47;
            {var subQ5=sQuery(id+"F4.wireOp",EDGE,"E32.0.left");Q47=makeQuery(id+"F4.imprint","IMPRINT",FACE,{"disambiguationData":[TD([[makeQuery(id+"F4.imprint","IMPRINT",EDGE,{"derivedFrom":subQ5}),-1.0]])]});}
            var Q48;
            {var subQ5=sQuery(id+"F4.wireOp",EDGE,"E32.0.right");Q48=makeQuery(id+"F4.imprint","IMPRINT",FACE,{"disambiguationData":[TD([[makeQuery(id+"F4.imprint","IMPRINT",EDGE,{"derivedFrom":subQ5}),1.0]])]});}
            var Q49;
            {var subQ0=sQuery(id+"F4.wireOp",EDGE,"E31");var subQ1=sQuery(id+"F4.wireOp",EDGE,"E30");var subQ2=makeQuery(id+"F4.imprint","INTERSECT",VERTEX,{"derivedFrom":[subQ1,subQ0]});Q49=makeQuery(id+"F4.imprint","IMPRINT",FACE,{"disambiguationData":[TD([[makeQuery(id+"F4.imprint","IMPRINT",EDGE,{"disambiguationData":[TD([[subQ2,1.0]])],"derivedFrom":subQ1}),1.0]])]});}
            var Q50;
            {var subQ0=sQuery(id+"F4.wireOp",EDGE,"E31");var subQ1=sQuery(id+"F4.wireOp",EDGE,"E30");var subQ2=makeQuery(id+"F4.imprint","INTERSECT",VERTEX,{"derivedFrom":[subQ1,subQ0]});Q50=makeQuery(id+"F4.imprint","IMPRINT",FACE,{"disambiguationData":[TD([[makeQuery(id+"F4.imprint","IMPRINT",EDGE,{"disambiguationData":[TD([[subQ2,1.0]])],"derivedFrom":subQ1}),-1.0]])]});}
            var Q51;
            {var subQ0=sQuery(id+"F4.wireOp",EDGE,"E31");var subQ1=sQuery(id+"F4.wireOp",EDGE,"E29");var subQ2=makeQuery(id+"F4.imprint","INTERSECT",VERTEX,{"derivedFrom":[subQ1,subQ0]});Q51=makeQuery(id+"F4.imprint","IMPRINT",FACE,{"disambiguationData":[TD([[makeQuery(id+"F4.imprint","IMPRINT",EDGE,{"disambiguationData":[TD([[subQ2,1.0]])],"derivedFrom":subQ1}),-1.0]])]});}
            var Q52;
            {var subQ0=sQuery(id+"F4.wireOp",EDGE,"E31");var subQ1=sQuery(id+"F4.wireOp",EDGE,"E29");var subQ2=makeQuery(id+"F4.imprint","INTERSECT",VERTEX,{"derivedFrom":[subQ1,subQ0]});Q52=makeQuery(id+"F4.imprint","IMPRINT",FACE,{"disambiguationData":[TD([[makeQuery(id+"F4.imprint","IMPRINT",EDGE,{"disambiguationData":[TD([[subQ2,1.0]])],"derivedFrom":subQ1}),1.0]])]});}
            var Q53;
            Q53=makeQuery(id+"F4.imprint","IMPRINT",FACE,{"disambiguationData":[TD([[makeQuery(id+"F4.imprint","IMPRINT",EDGE,{"derivedFrom":sQuery(id+"F4.wireOp",EDGE,"E21.2.startCap")}),-1.0]])]});
            var Q54;
            Q54=makeQuery(id+"F4.imprint","IMPRINT",FACE,{"disambiguationData":[TD([[makeQuery(id+"F4.imprint","IMPRINT",EDGE,{"derivedFrom":sQuery(id+"F4.wireOp",EDGE,"E21.1.startCap")}),-1.0]])]});
            var Q55;
            Q55=makeQuery(id+"F4.imprint","IMPRINT",FACE,{"disambiguationData":[TD([[makeQuery(id+"F4.imprint","IMPRINT",EDGE,{"derivedFrom":sQuery(id+"F4.wireOp",EDGE,"E24.bottom")}),1.0]])]});
            var Q56;
            Q56=makeQuery(id+"F4.imprint","IMPRINT",FACE,{"disambiguationData":[TD([[makeQuery(id+"F4.imprint","IMPRINT",EDGE,{"derivedFrom":sQuery(id+"F4.wireOp",EDGE,"E23")}),1.0]])]});
            var Q57;
            Q57=makeQuery(id+"F4.imprint","IMPRINT",FACE,{"disambiguationData":[TD([[makeQuery(id+"F4.imprint","IMPRINT",EDGE,{"derivedFrom":sQuery(id+"F4.wireOp",EDGE,"E22")}),1.0]])]});
            var Q58;
            {var subQ0=sQuery(id+"F4.wireOp",EDGE,"E20");var subQ1=sQuery(id+"F4.wireOp",EDGE,"E18");var subQ2=makeQuery(id+"F4.imprint","INTERSECT",VERTEX,{"derivedFrom":[subQ1,subQ0]});Q58=makeQuery(id+"F4.imprint","IMPRINT",FACE,{"disambiguationData":[TD([[makeQuery(id+"F4.imprint","IMPRINT",EDGE,{"disambiguationData":[TD([[subQ2,1.0]])],"derivedFrom":subQ1}),1.0]])]});}
            var Q59;
            {var subQ0=sQuery(id+"F4.wireOp",EDGE,"E20");var subQ1=sQuery(id+"F4.wireOp",EDGE,"E18");var subQ2=makeQuery(id+"F4.imprint","INTERSECT",VERTEX,{"derivedFrom":[subQ1,subQ0]});Q59=makeQuery(id+"F4.imprint","IMPRINT",FACE,{"disambiguationData":[TD([[makeQuery(id+"F4.imprint","IMPRINT",EDGE,{"disambiguationData":[TD([[subQ2,1.0]])],"derivedFrom":subQ1}),-1.0]])]});}
            var Q60;
            {var subQ0=sQuery(id+"F4.wireOp",EDGE,"E20");var subQ1=sQuery(id+"F4.wireOp",EDGE,"E19");var subQ2=makeQuery(id+"F4.imprint","INTERSECT",VERTEX,{"derivedFrom":[subQ1,subQ0]});Q60=makeQuery(id+"F4.imprint","IMPRINT",FACE,{"disambiguationData":[TD([[makeQuery(id+"F4.imprint","IMPRINT",EDGE,{"disambiguationData":[TD([[subQ2,1.0]])],"derivedFrom":subQ1}),1.0]])]});}
            var Q61;
            {var subQ0=sQuery(id+"F4.wireOp",EDGE,"E20");var subQ1=sQuery(id+"F4.wireOp",EDGE,"E19");var subQ2=makeQuery(id+"F4.imprint","INTERSECT",VERTEX,{"derivedFrom":[subQ1,subQ0]});Q61=makeQuery(id+"F4.imprint","IMPRINT",FACE,{"disambiguationData":[TD([[makeQuery(id+"F4.imprint","IMPRINT",EDGE,{"disambiguationData":[TD([[subQ2,1.0]])],"derivedFrom":subQ1}),-1.0]])]});}
            var Q62;
            {var subQ5=sQuery(id+"F4.wireOp",EDGE,"E21.0.left");Q62=makeQuery(id+"F4.imprint","IMPRINT",FACE,{"disambiguationData":[TD([[makeQuery(id+"F4.imprint","IMPRINT",EDGE,{"derivedFrom":subQ5}),-1.0]])]});}
            var Q63;
            {var subQ5=sQuery(id+"F4.wireOp",EDGE,"E21.0.right");Q63=makeQuery(id+"F4.imprint","IMPRINT",FACE,{"disambiguationData":[TD([[makeQuery(id+"F4.imprint","IMPRINT",EDGE,{"derivedFrom":subQ5}),1.0]])]});}
            extrude(context, id + "F5", {"entities" : qUnion([Q0, Q1, Q2, Q3, Q4, Q5, Q6, Q7, Q8, Q9, Q10, Q11, Q12, Q13, Q14, Q15, Q16, Q17, Q18, Q19, Q20, Q21, Q22, Q23, Q24, Q25, Q26, Q27, Q28, Q29, Q30, Q31, Q32, Q33, Q34, Q35, Q36, Q37, Q38, Q39, Q40, Q41, Q42, Q43, Q44, Q45, Q46, Q47, Q48, Q49, Q50, Q51, Q52, Q53, Q54, Q55, Q56, Q57, Q58, Q59, Q60, Q61, Q62, Q63]), "operationType" : NewBodyOperationType.REMOVE, "depth" : 25 * mm});
        }
    });
